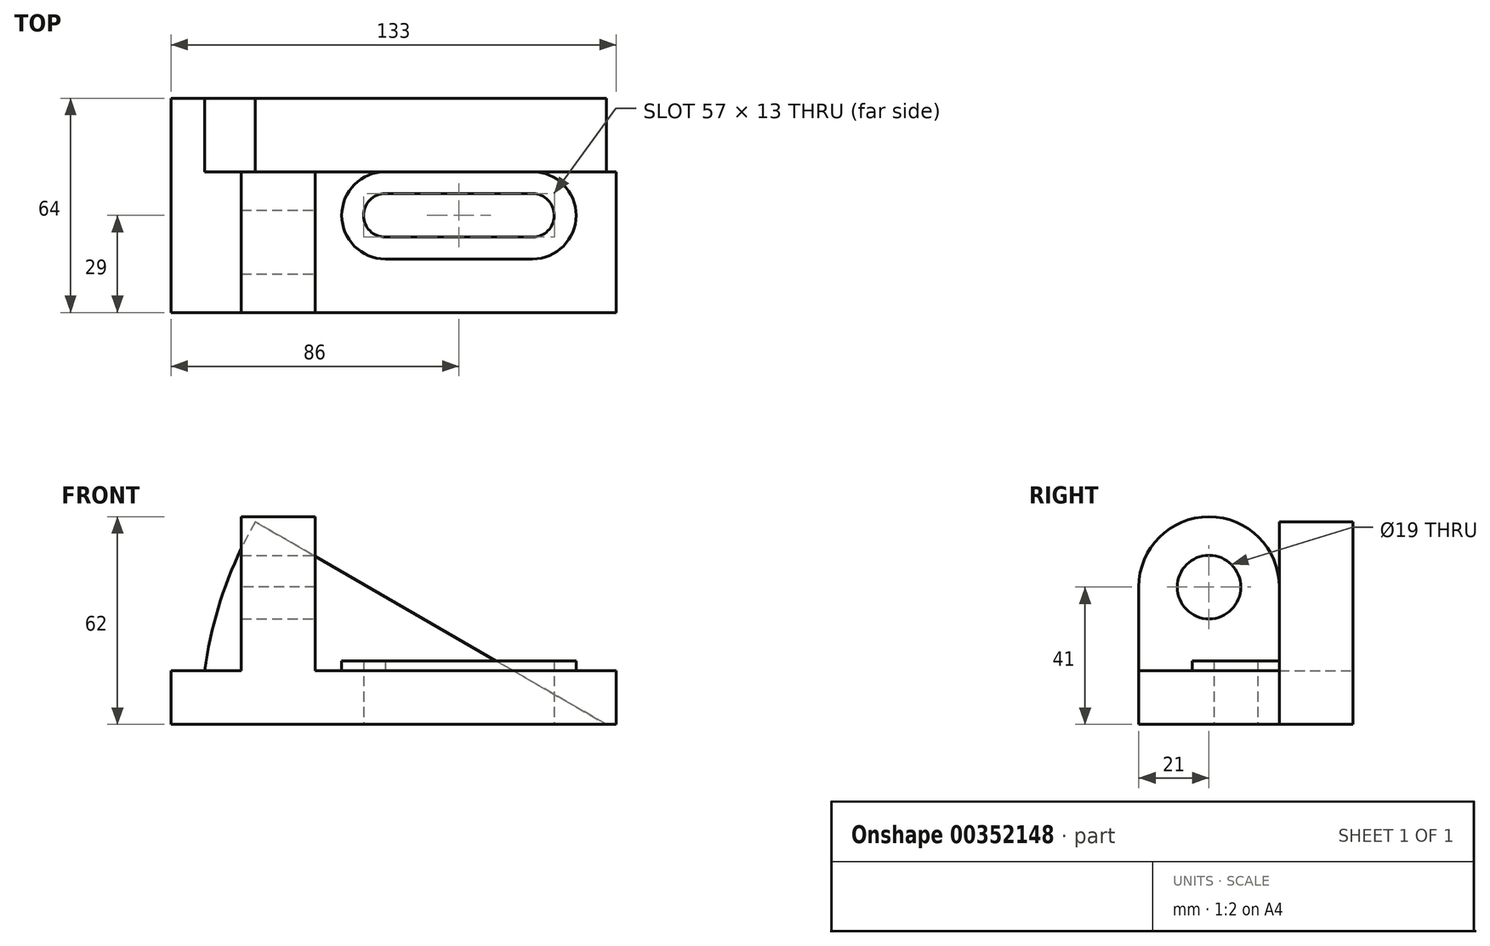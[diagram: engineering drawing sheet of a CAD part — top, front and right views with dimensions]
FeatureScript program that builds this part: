
annotation { "Feature Type Name" : "Feature", "Feature Type Description" : "" }
export const myFeature = defineFeature(function(context is Context, id is Id, definition is map)
    precondition{}
    {
        {
            var Q0;
            Q0=qCreatedBy(makeId("Front.planeOp"),FACE);
            var sketch = newSketch(context, id + "F0", { "sketchPlane" : qUnion([Q0])});
            skLineSegment(sketch, "E0", {"start": v(0, 0) * mm, "end": v(133, 0) * mm});
            skLineSegment(sketch, "E1", {"start": v(133, 0) * mm, "end": v(133, 16) * mm});
            skLineSegment(sketch, "E2", {"start": v(133, 16) * mm, "end": v(43, 16) * mm});
            skLineSegment(sketch, "E3", {"start": v(43, 16) * mm, "end": v(43, 41) * mm});
            skLineSegment(sketch, "E4", {"start": v(43, 41) * mm, "end": v(21, 41) * mm});
            skLineSegment(sketch, "E5", {"start": v(21, 41) * mm, "end": v(21, 16) * mm});
            skLineSegment(sketch, "E6", {"start": v(21, 16) * mm, "end": v(0, 16) * mm});
            skLineSegment(sketch, "E7", {"start": v(0, 16) * mm, "end": v(0, 0) * mm});
            skSolve(sketch);
        }
        {
            var Q0;
            Q0=makeQuery(id+"F0.imprint","IMPRINT",FACE,{"disambiguationData":[TD([[makeQuery(id+"F0.imprint","IMPRINT",EDGE,{"derivedFrom":sQuery(id+"F0.wireOp",EDGE,"E0")}),1.0]])]});
            extrude(context, id + "F1", {"entities" : qUnion([Q0]), "oppositeDirection" : true, "depth" : 42 * mm});
        }
        {
            var Q0;
            Q0=qCreatedBy(makeId("Top.planeOp"),FACE);
            var sketch = newSketch(context, id + "F2", { "sketchPlane" : qUnion([Q0])});
            skLineSegment(sketch, "E8", {"start": v(130, 42) * mm, "end": v(130, 64) * mm});
            skLineSegment(sketch, "E9", {"start": v(130, 64) * mm, "end": v(9, 64) * mm});
            skLineSegment(sketch, "E10", {"start": v(9, 64) * mm, "end": v(9, 42) * mm});
            skLineSegment(sketch, "E11", {"start": v(9, 42) * mm, "end": v(130, 42) * mm});
            skSolve(sketch);
        }
        {
            var Q0;
            Q0=makeQuery(id+"F2.imprint","IMPRINT",FACE,{"disambiguationData":[TD([[makeQuery(id+"F2.imprint","IMPRINT",EDGE,{"derivedFrom":sQuery(id+"F2.wireOp",EDGE,"E8")}),1.0]])]});
            var Q1;
            Q1=sQuery(id+"F2.wireOp",EDGE,"E8");
            revolve(context, id + "F3", {"operationType" : NewBodyOperationType.ADD, "entities" : qUnion([Q0]), "axis" : qUnion([Q1]), "revolveType" : RevolveType.ONE_DIRECTION, "angle" : 30 * degree});
        }
        {
            var Q0;
            Q0=makeQuery(id+"F1.opExtrude","SWEPT_FACE",FACE,{"disambiguationData":[OSD([sQuery(id+"F0.wireOp",EDGE,"E3")])]});
            var sketch = newSketch(context, id + "F4", { "sketchPlane" : qUnion([Q0])});
            skArc(sketch, "E12", {"start": v(42, 41) * mm, "mid": v(21, 62) * mm, "end": v(0, 41) * mm});
            skSolve(sketch);
        }
        {
            var Q0;
            Q0=makeQuery(id+"F4.imprint","IMPRINT",FACE,{"disambiguationData":[TD([[makeQuery(id+"F4.imprint","IMPRINT",EDGE,{"derivedFrom":sQuery(id+"F4.wireOp",EDGE,"E12")}),1.0]])]});
            extrude(context, id + "F5", {"entities" : qUnion([Q0]), "operationType" : NewBodyOperationType.ADD, "oppositeDirection" : true, "depth" : 22 * mm});
        }
        {
            var Q0;
            {var subQ0=sQuery(id+"F0.wireOp",EDGE,"E3");Q0=makeQuery(id+"F5.boolean.opBoolean","MERGE",FACE,{"derivedFrom":[makeQuery(id+"F1.opExtrude","SWEPT_FACE",FACE,{"disambiguationData":[OSD([subQ0])]}),makeQuery(id+"F5.opExtrude","CAP_FACE",FACE,{"disambiguationData":[OSD([subQ0,sQuery(id+"F0.wireOp",EDGE,"E4"),sQuery(id+"F4.wireOp",EDGE,"E12")])],"isStart":true})]});}
            var sketch = newSketch(context, id + "F6", { "sketchPlane" : qUnion([Q0])});
            skCircle(sketch, "E13", {"center": v(21, 41) * mm, "radius": 9.5 * mm});
            skSolve(sketch);
        }
        {
            var Q0;
            Q0=makeQuery(id+"F1.opExtrude","SWEPT_FACE",FACE,{"disambiguationData":[OSD([sQuery(id+"F0.wireOp",EDGE,"E2")])]});
            var sketch = newSketch(context, id + "F7", { "sketchPlane" : qUnion([Q0])});
            skArc(sketch, "E14", {"start": v(64, 35.5) * mm, "mid": v(57.5, 29) * mm, "end": v(64, 22.5) * mm});
            skArc(sketch, "E15", {"start": v(108, 22.5) * mm, "mid": v(114.5, 29) * mm, "end": v(108, 35.5) * mm});
            skLineSegment(sketch, "E16", {"start": v(64, 35.5) * mm, "end": v(108, 35.5) * mm});
            skLineSegment(sketch, "E17", {"start": v(64, 22.5) * mm, "end": v(108, 22.5) * mm});
            skArc(sketch, "E18", {"start": v(64, 42) * mm, "mid": v(51, 29) * mm, "end": v(64, 16) * mm});
            skArc(sketch, "E19", {"start": v(108, 16) * mm, "mid": v(121, 29) * mm, "end": v(108, 42) * mm});
            skLineSegment(sketch, "E20", {"start": v(64, 42) * mm, "end": v(108, 42) * mm});
            skLineSegment(sketch, "E21", {"start": v(64, 16) * mm, "end": v(108, 16) * mm});
            skSolve(sketch);
        }
        {
            var Q0;
            Q0=makeQuery(id+"F7.imprint","IMPRINT",FACE,{"disambiguationData":[TD([[makeQuery(id+"F7.imprint","IMPRINT",EDGE,{"derivedFrom":sQuery(id+"F7.wireOp",EDGE,"E14")}),-1.0]])]});
            extrude(context, id + "F8", {"entities" : qUnion([Q0]), "operationType" : NewBodyOperationType.ADD, "depth" : 3 * mm});
        }
        {
            var Q0;
            Q0=makeQuery(id+"F8.boolean.opBoolean","SPLIT",FACE,{"disambiguationData":[TD([makeQuery(id+"F8.opExtrude","SWEPT_FACE",FACE,{"disambiguationData":[OSD([sQuery(id+"F7.wireOp",EDGE,"E14")])]})])],"derivedFrom":makeQuery(id+"F1.opExtrude","SWEPT_FACE",FACE,{"disambiguationData":[OSD([sQuery(id+"F0.wireOp",EDGE,"E2")])]})});
            extrude(context, id + "F9", {"entities" : qUnion([Q0]), "operationType" : NewBodyOperationType.REMOVE, "oppositeDirection" : true, "depth" : 25 * mm});
        }
        {
            var Q0;
            Q0=makeQuery(id+"F6.imprint","IMPRINT",FACE,{"disambiguationData":[TD([[makeQuery(id+"F6.imprint","IMPRINT",EDGE,{"derivedFrom":sQuery(id+"F6.wireOp",EDGE,"E13")}),1.0]])]});
            extrude(context, id + "F10", {"entities" : qUnion([Q0]), "operationType" : NewBodyOperationType.REMOVE, "oppositeDirection" : true, "depth" : 25 * mm});
        }
        {
            var Q0;
            Q0=makeQuery(id+"F1.opExtrude","SWEPT_FACE",FACE,{"disambiguationData":[OSD([sQuery(id+"F0.wireOp",EDGE,"E6")])]});
            var sketch = newSketch(context, id + "F11", { "sketchPlane" : qUnion([Q0])});
            skLineSegment(sketch, "E22", {"start": v(0, 42) * mm, "end": v(0, 64) * mm});
            skLineSegment(sketch, "E23", {"start": v(10.06, 42) * mm, "end": v(10.06, 64) * mm});
            skLineSegment(sketch, "E24", {"start": v(10.06, 64) * mm, "end": v(0, 64) * mm});
            skSolve(sketch);
        }
        {
            var Q0;
            Q0=makeQuery(id+"F11.imprint","IMPRINT",FACE,{"disambiguationData":[TD([[makeQuery(id+"F11.imprint","IMPRINT",EDGE,{"derivedFrom":sQuery(id+"F11.wireOp",EDGE,"E22")}),-1.0]])]});
            extrude(context, id + "F12", {"entities" : qUnion([Q0]), "operationType" : NewBodyOperationType.ADD, "oppositeDirection" : true, "depth" : 16 * mm});
        }
    });
